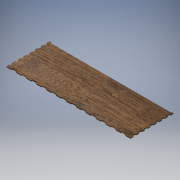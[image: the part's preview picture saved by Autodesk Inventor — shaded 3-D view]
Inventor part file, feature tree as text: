
AUTODESK INVENTOR PART (.ipt)
format: ipt  version: 2018.3 (Build 223284000, 284)  size: 1,501,696 bytes
history: native  units: mm
features: other x12, reference x7, extrude x5, sketch x5
ambient origin geometry x8: Origin, YZ Plane, XZ Plane, XY Plane, X Axis, Y Axis, Z Axis, Center Point
bodies: Solido1 (feature_tree)
feature tree (29):
  extrude  "Estrusione1"  Depth=467.0mm
  extrude  "Estrusione2"  Depth=157.0mm
  extrude  "Estrusione3"  Depth=4.0mm TaperAngle=0.0deg
  extrude  "Estrusione4"  Depth=4.0mm
  extrude  "Estrusione5"  Depth=475.0mm
  sketch  "Schizzo1"
  sketch  "Schizzo3"
  other  "Linea chiusa proiettata2"
  sketch  "Schizzo4"
  reference  "Riferimento1"
  reference  "Riferimento2"
  reference  "Riferimento3"
  reference  "Riferimento4"
  reference  "Riferimento5"
  reference  "Riferimento6"
  reference  "Riferimento7"
  sketch  "Schizzo5"
  other  "Linea chiusa proiettata3"
  sketch  "Schizzo6"
  other  "<userpath>\Desktop\Scorbot Hardware\Case Board\caseHw.iam"
  other  "caseHw.iam"
  other  "matherBoard v1:1"
  other  "PCB Component:1"
  other  "Board:1"
  other  "Raspberry Pi 3:1"
  other  "Raspberry Pi 347_115"
  other  "Raspberry Pi 345_113"
  other  "Raspberry Pi 349_117"
  other  "Raspberry Pi 351_119"
